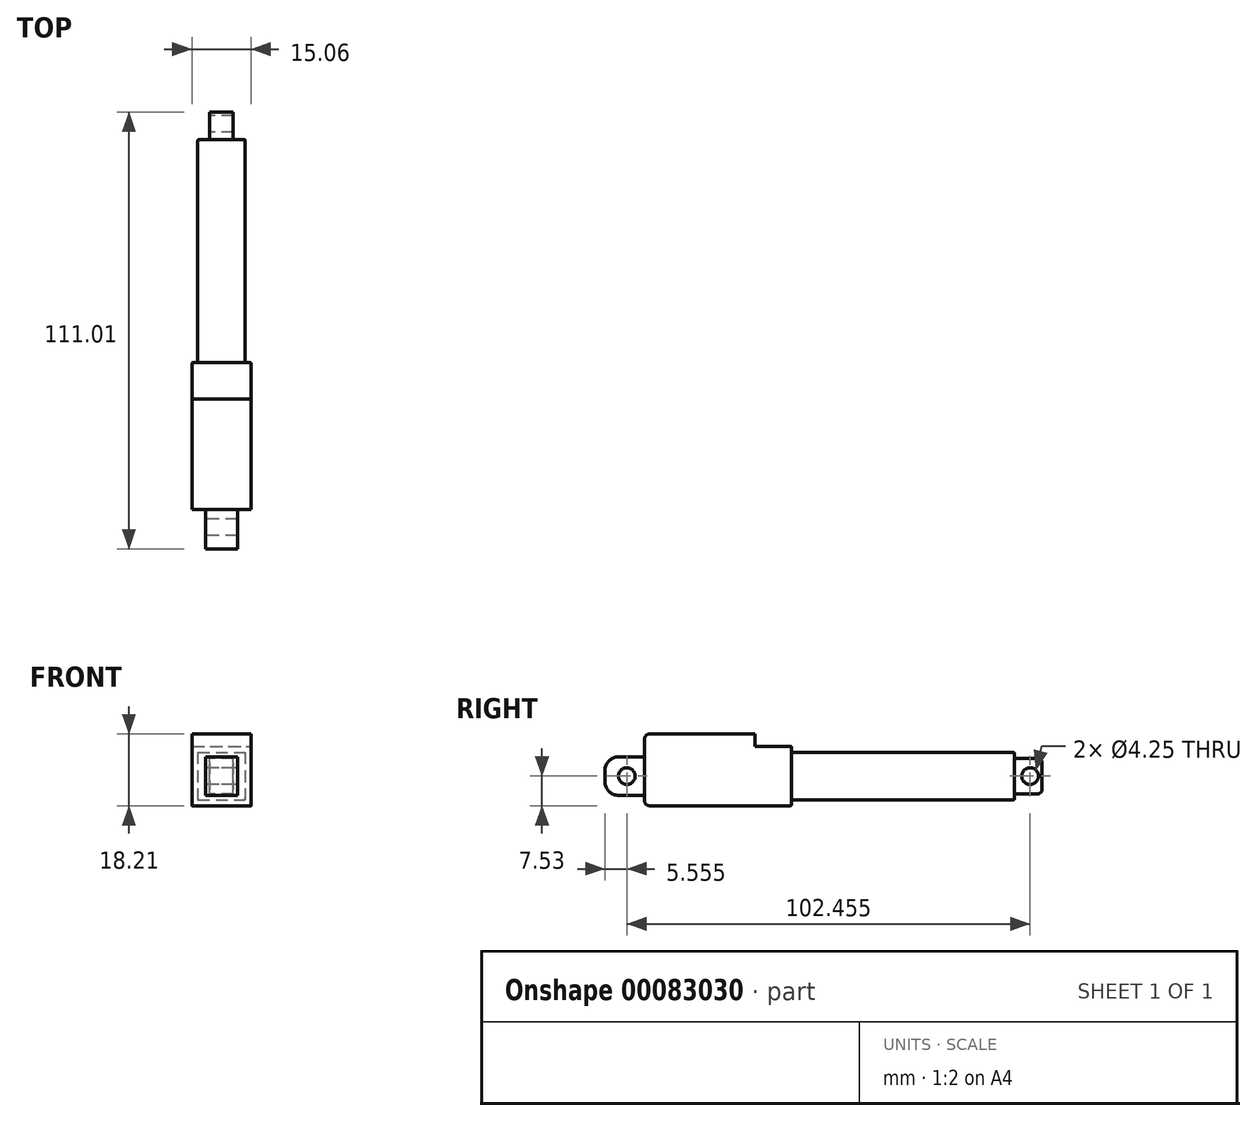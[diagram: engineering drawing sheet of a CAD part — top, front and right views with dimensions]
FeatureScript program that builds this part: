
annotation { "Feature Type Name" : "Feature", "Feature Type Description" : "" }
export const myFeature = defineFeature(function(context is Context, id is Id, definition is map)
    precondition{}
    {
        {
            var Q0;
            Q0=qCreatedBy(makeId("Front.planeOp"),FACE);
            var sketch = newSketch(context, id + "F0", { "sketchPlane" : qUnion([Q0])});
            skLineSegment(sketch, "E0.bottom", {"start": v(-6.03, 6.03) * mm, "end": v(6.03, 6.03) * mm});
            skLineSegment(sketch, "E0.top", {"start": v(-6.03, -6.03) * mm, "end": v(6.03, -6.03) * mm});
            skLineSegment(sketch, "E0.left", {"start": v(-6.03, 6.03) * mm, "end": v(-6.03, -6.03) * mm});
            skLineSegment(sketch, "E0.right", {"start": v(6.03, 6.03) * mm, "end": v(6.03, -6.03) * mm});
            skSolve(sketch);
        }
        {
            var Q0;
            Q0=makeQuery(id+"F0.imprint","IMPRINT",FACE,{"disambiguationData":[TD([[makeQuery(id+"F0.imprint","IMPRINT",EDGE,{"derivedFrom":sQuery(id+"F0.wireOp",EDGE,"E0.bottom")}),-1.0]])]});
            extrude(context, id + "F1", {"entities" : qUnion([Q0]), "depth" : 56.64 * mm});
        }
        {
            var Q0;
            Q0=makeQuery(id+"F1.opExtrude","CAP_FACE",FACE,{"disambiguationData":[OSD([sQuery(id+"F0.wireOp",EDGE,"E0.bottom"),sQuery(id+"F0.wireOp",EDGE,"E0.top"),sQuery(id+"F0.wireOp",EDGE,"E0.left"),sQuery(id+"F0.wireOp",EDGE,"E0.right")])],"isStart":false});
            var sketch = newSketch(context, id + "F2", { "sketchPlane" : qUnion([Q0])});
            skLineSegment(sketch, "E1.bottom", {"start": v(-7.53, 7.53) * mm, "end": v(7.53, 7.53) * mm});
            skLineSegment(sketch, "E1.top", {"start": v(-7.53, -7.53) * mm, "end": v(7.53, -7.53) * mm});
            skLineSegment(sketch, "E1.left", {"start": v(-7.53, 7.53) * mm, "end": v(-7.53, -7.53) * mm});
            skLineSegment(sketch, "E1.right", {"start": v(7.53, 7.53) * mm, "end": v(7.53, -7.53) * mm});
            skSolve(sketch);
        }
        {
            var Q0;
            Q0=makeQuery(id+"F2.imprint","IMPRINT",FACE,{"disambiguationData":[TD([[makeQuery(id+"F2.imprint","IMPRINT",EDGE,{"derivedFrom":sQuery(id+"F2.wireOp",EDGE,"E1.bottom")}),-1.0]])]});
            var Q1;
            Q1=makeQuery(id+"F2.imprint","IMPRINT",FACE,{"disambiguationData":[TD([[makeQuery(id+"F2.imprint","IMPRINT",EDGE,{"derivedFrom":makeQuery(id+"F1.opExtrude","CAP_EDGE",EDGE,{"disambiguationData":[OSD([sQuery(id+"F0.wireOp",EDGE,"E0.bottom")])],"isStart":false})}),-1.0]])]});
            extrude(context, id + "F3", {"entities" : qUnion([Q0, Q1]), "operationType" : NewBodyOperationType.ADD, "depth" : 37.31 * mm});
        }
        {
            var Q0;
            Q0=makeQuery(id+"F3.opExtrude","CAP_FACE",FACE,{"disambiguationData":[OSD([sQuery(id+"F2.wireOp",EDGE,"E1.bottom"),sQuery(id+"F2.wireOp",EDGE,"E1.top"),sQuery(id+"F2.wireOp",EDGE,"E1.left"),sQuery(id+"F2.wireOp",EDGE,"E1.right")])],"isStart":true});
            var sketch = newSketch(context, id + "F4", { "sketchPlane" : qUnion([Q0])});
            skLineSegment(sketch, "E2.bottom", {"start": v(-7.53, 7.53) * mm, "end": v(7.53, 7.53) * mm});
            skLineSegment(sketch, "E2.top", {"start": v(-7.53, 10.68) * mm, "end": v(7.53, 10.68) * mm});
            skLineSegment(sketch, "E2.left", {"start": v(-7.53, 7.53) * mm, "end": v(-7.53, 10.68) * mm});
            skLineSegment(sketch, "E2.right", {"start": v(7.53, 7.53) * mm, "end": v(7.53, 10.68) * mm});
            skSolve(sketch);
        }
        {
            var Q0;
            Q0=makeQuery(id+"F4.imprint","IMPRINT",FACE,{"disambiguationData":[TD([[makeQuery(id+"F4.imprint","IMPRINT",EDGE,{"derivedFrom":sQuery(id+"F4.wireOp",EDGE,"E2.bottom")}),-1.0]])]});
            var Q1;
            Q1=makeQuery(id+"F3.opExtrude","CAP_FACE",FACE,{"disambiguationData":[OSD([sQuery(id+"F2.wireOp",EDGE,"E1.bottom"),sQuery(id+"F2.wireOp",EDGE,"E1.top"),sQuery(id+"F2.wireOp",EDGE,"E1.left"),sQuery(id+"F2.wireOp",EDGE,"E1.right")])],"isStart":false});
            extrude(context, id + "F5", {"entities" : qUnion([Q0]), "operationType" : NewBodyOperationType.ADD, "endBound" : BoundingType.UP_TO_SURFACE, "oppositeDirection" : true, "endBoundEntityFace" : qUnion([Q1]), "depth" : 25.4 * mm});
        }
        {
            var Q0;
            Q0=makeQuery(id+"F5.boolean.opBoolean","MERGE",FACE,{"derivedFrom":[makeQuery(id+"F3.opExtrude","SWEPT_FACE",FACE,{"disambiguationData":[OSD([sQuery(id+"F2.wireOp",EDGE,"E1.right")])]}),makeQuery(id+"F5.opExtrude","SWEPT_FACE",FACE,{"disambiguationData":[OSD([sQuery(id+"F4.wireOp",EDGE,"E2.left")])]})]});
            var sketch = newSketch(context, id + "F6", { "sketchPlane" : qUnion([Q0])});
            skPoint(sketch, "E3.0", {"position": v(-56.64, 6.03) * mm});
            skPoint(sketch, "E4.0", {"position": v(-56.64, 10.68) * mm});
            skLineSegment(sketch, "E5", {"start": v(-65.84, 10.68) * mm, "end": v(-65.84, 7.53) * mm});
            skPoint(sketch, "E6.0", {"position": v(-56.64, -6.03) * mm});
            skPoint(sketch, "E7.0", {"position": v(-56.64, -7.53) * mm});
            skPoint(sketch, "E8", {"position": v(-56.64, 7.53) * mm});
            skLineSegment(sketch, "E9", {"start": v(-65.84, 7.53) * mm, "end": v(-56.64, 7.53) * mm});
            skPoint(sketch, "E9.startSnap0", {"position": v(-65.84, 8.36) * mm});
            skLineSegment(sketch, "E10", {"start": v(-56.64, 7.53) * mm, "end": v(-56.64, 10.68) * mm});
            skLineSegment(sketch, "E11", {"start": v(-56.64, 10.68) * mm, "end": v(-65.84, 10.68) * mm});
            skPoint(sketch, "E12.start.orphan", {"position": v(-65.84, 6.03) * mm});
            skSolve(sketch);
        }
        {
            var Q0;
            Q0=makeQuery(id+"F6.imprint","IMPRINT",FACE,{"disambiguationData":[TD([[makeQuery(id+"F6.imprint","IMPRINT",EDGE,{"derivedFrom":sQuery(id+"F6.wireOp",EDGE,"E5")}),1.0]])]});
            extrude(context, id + "F7", {"entities" : qUnion([Q0]), "operationType" : NewBodyOperationType.REMOVE, "oppositeDirection" : true, "depth" : 254 * mm});
        }
        {
            var Q0;
            Q0=makeQuery(id+"F7.boolean.opBoolean","COPY",EDGE,{"derivedFrom":makeQuery(id+"F7.opExtrude","SWEPT_EDGE",EDGE,{"disambiguationData":[OSD([sQuery(id+"F2.wireOp",EDGE,"E1.right"),sQuery(id+"F4.wireOp",EDGE,"E2.left"),sQuery(id+"F6.wireOp",EDGE,"E9"),sQuery(id+"F6.wireOp",EDGE,"E10")])]})});
            var Q1;
            Q1=makeQuery(id+"F5.boolean.opBoolean","MERGE",EDGE,{"derivedFrom":[makeQuery(id+"F3.opExtrude","CAP_EDGE",EDGE,{"disambiguationData":[OSD([sQuery(id+"F2.wireOp",EDGE,"E1.right")])],"isStart":true}),makeQuery(id+"F5.opExtrude","CAP_EDGE",EDGE,{"disambiguationData":[OSD([sQuery(id+"F4.wireOp",EDGE,"E2.left")])],"isStart":true})]});
            var Q2;
            Q2=makeQuery(id+"F3.opExtrude","CAP_EDGE",EDGE,{"disambiguationData":[OSD([sQuery(id+"F2.wireOp",EDGE,"E1.top")])],"isStart":true});
            var Q3;
            Q3=makeQuery(id+"F5.boolean.opBoolean","MERGE",EDGE,{"derivedFrom":[makeQuery(id+"F3.opExtrude","CAP_EDGE",EDGE,{"disambiguationData":[OSD([sQuery(id+"F2.wireOp",EDGE,"E1.left")])],"isStart":true}),makeQuery(id+"F5.opExtrude","CAP_EDGE",EDGE,{"disambiguationData":[OSD([sQuery(id+"F4.wireOp",EDGE,"E2.right")])],"isStart":true})]});
            var Q4;
            Q4=makeQuery(id+"F1.opExtrude","CAP_EDGE",EDGE,{"disambiguationData":[OSD([sQuery(id+"F0.wireOp",EDGE,"E0.left")])],"isStart":true});
            var Q5;
            Q5=makeQuery(id+"F1.opExtrude","CAP_EDGE",EDGE,{"disambiguationData":[OSD([sQuery(id+"F0.wireOp",EDGE,"E0.bottom")])],"isStart":true});
            var Q6;
            Q6=makeQuery(id+"F1.opExtrude","CAP_EDGE",EDGE,{"disambiguationData":[OSD([sQuery(id+"F0.wireOp",EDGE,"E0.right")])],"isStart":true});
            var Q7;
            Q7=makeQuery(id+"F1.opExtrude","CAP_EDGE",EDGE,{"disambiguationData":[OSD([sQuery(id+"F0.wireOp",EDGE,"E0.top")])],"isStart":true});
            fillet(context, id + "F8", {"entities" : qUnion([Q0, Q1, Q2, Q3, Q4, Q5, Q6, Q7]), "radius" : 0.25 * mm, "tangentPropagation" : true, "allowEdgeOverflow" : false});
        }
        {
            var Q0;
            Q0=makeQuery(id+"F7.boolean.opBoolean","COPY",EDGE,{"derivedFrom":makeQuery(id+"F7.opExtrude","SWEPT_EDGE",EDGE,{"disambiguationData":[OSD([sQuery(id+"F4.wireOp",EDGE,"E2.top"),sQuery(id+"F4.wireOp",EDGE,"E2.left"),sQuery(id+"F6.wireOp",EDGE,"E5"),sQuery(id+"F6.wireOp",EDGE,"E11")])]})});
            var Q1;
            Q1=makeQuery(id+"F5.opExtrude","CAP_EDGE",EDGE,{"disambiguationData":[OSD([sQuery(id+"F4.wireOp",EDGE,"E2.top")])],"isStart":false});
            var Q2;
            Q2=makeQuery(id+"F3.opExtrude","CAP_EDGE",EDGE,{"disambiguationData":[OSD([sQuery(id+"F2.wireOp",EDGE,"E1.top")])],"isStart":false});
            fillet(context, id + "F9", {"entities" : qUnion([Q0, Q1, Q2]), "radius" : 1.27 * mm, "tangentPropagation" : true, "allowEdgeOverflow" : false});
        }
        {
            var Q0;
            Q0=makeQuery(id+"F5.boolean.opBoolean","MERGE",FACE,{"derivedFrom":[makeQuery(id+"F3.opExtrude","CAP_FACE",FACE,{"disambiguationData":[OSD([sQuery(id+"F2.wireOp",EDGE,"E1.bottom"),sQuery(id+"F2.wireOp",EDGE,"E1.top"),sQuery(id+"F2.wireOp",EDGE,"E1.left"),sQuery(id+"F2.wireOp",EDGE,"E1.right")])],"isStart":false}),makeQuery(id+"F5.opExtrude","CAP_FACE",FACE,{"disambiguationData":[OSD([sQuery(id+"F4.wireOp",EDGE,"E2.bottom"),sQuery(id+"F4.wireOp",EDGE,"E2.top"),sQuery(id+"F4.wireOp",EDGE,"E2.left"),sQuery(id+"F4.wireOp",EDGE,"E2.right")])],"isStart":false})]});
            var sketch = newSketch(context, id + "F10", { "sketchPlane" : qUnion([Q0])});
            skLineSegment(sketch, "E13.bottom", {"start": v(-4.04, 4.89) * mm, "end": v(4.04, 4.89) * mm});
            skLineSegment(sketch, "E13.top", {"start": v(-4.04, -4.89) * mm, "end": v(4.04, -4.89) * mm});
            skLineSegment(sketch, "E13.left", {"start": v(-4.04, 4.89) * mm, "end": v(-4.04, -4.89) * mm});
            skLineSegment(sketch, "E13.right", {"start": v(4.04, 4.89) * mm, "end": v(4.04, -4.89) * mm});
            skSolve(sketch);
        }
        {
            var Q0;
            Q0=makeQuery(id+"F10.imprint","IMPRINT",FACE,{"disambiguationData":[TD([[makeQuery(id+"F10.imprint","IMPRINT",EDGE,{"derivedFrom":sQuery(id+"F10.wireOp",EDGE,"E13.bottom")}),-1.0]])]});
            extrude(context, id + "F11", {"entities" : qUnion([Q0]), "operationType" : NewBodyOperationType.ADD, "depth" : 10.06 * mm});
        }
        {
            var Q0;
            Q0=makeQuery(id+"F11.opExtrude","SWEPT_FACE",FACE,{"disambiguationData":[OSD([sQuery(id+"F10.wireOp",EDGE,"E13.left")])]});
            var sketch = newSketch(context, id + "F12", { "sketchPlane" : qUnion([Q0])});
            skLineSegment(sketch, "E14.0", {"start": v(93.95, 9.41) * mm, "end": v(93.95, -6.26) * mm});
            skLineSegment(sketch, "E15", {"start": v(93.95, 0) * mm, "end": v(98.45, 0) * mm, "construction": true});
            skPoint(sketch, "E15.endSnap0", {"position": v(93.95, 0) * mm});
            skCircle(sketch, "E16", {"center": v(98.45, 0) * mm, "radius": 2.12 * mm});
            skSolve(sketch);
        }
        {
            var Q0;
            Q0=makeQuery(id+"F12.imprint","IMPRINT",FACE,{"disambiguationData":[TD([[makeQuery(id+"F12.imprint","IMPRINT",EDGE,{"derivedFrom":sQuery(id+"F12.wireOp",EDGE,"E16")}),1.0]])]});
            extrude(context, id + "F13", {"entities" : qUnion([Q0]), "operationType" : NewBodyOperationType.REMOVE, "oppositeDirection" : true, "depth" : 25 * mm});
        }
        {
            var Q0;
            Q0=makeQuery(id+"F11.opExtrude","CAP_EDGE",EDGE,{"disambiguationData":[OSD([sQuery(id+"F10.wireOp",EDGE,"E13.bottom")])],"isStart":false});
            var Q1;
            Q1=makeQuery(id+"F11.opExtrude","CAP_EDGE",EDGE,{"disambiguationData":[OSD([sQuery(id+"F10.wireOp",EDGE,"E13.top")])],"isStart":false});
            fillet(context, id + "F14", {"entities" : qUnion([Q0, Q1]), "radius" : 3.5 * mm, "tangentPropagation" : true, "allowEdgeOverflow" : false});
        }
        {
            var Q0;
            Q0=makeQuery(id+"F1.opExtrude","SWEPT_FACE",FACE,{"disambiguationData":[OSD([sQuery(id+"F0.wireOp",EDGE,"E0.left")])]});
            var sketch = newSketch(context, id + "F15", { "sketchPlane" : qUnion([Q0])});
            skArc(sketch, "E17.0.0", {"start": v(0.25, 6.03) * mm, "mid": v(0.07, 5.96) * mm, "end": v(0, 5.78) * mm});
            skLineSegment(sketch, "E17.0.1", {"start": v(0, -5.78) * mm, "end": v(0, 5.78) * mm});
            skArc(sketch, "E17.0.2", {"start": v(0, -5.78) * mm, "mid": v(0.07, -5.96) * mm, "end": v(0.25, -6.03) * mm});
            skLineSegment(sketch, "E17.0.3", {"start": v(0.25, -6.03) * mm, "end": v(0.25, 6.03) * mm});
            skLineSegment(sketch, "E18.0", {"start": v(104.01, 1.39) * mm, "end": v(104.01, -1.39) * mm});
            skCircle(sketch, "E19.0", {"center": v(98.45, 0) * mm, "radius": 2.12 * mm});
            skSolve(sketch);
        }
        {
            var Q0;
            Q0=qCreatedBy(makeId("Right.planeOp"),FACE);
            var sketch = newSketch(context, id + "F16", { "sketchPlane" : qUnion([Q0])});
            skLineSegment(sketch, "E20.0", {"start": v(0, -5.78) * mm, "end": v(0, 5.78) * mm});
            skLineSegment(sketch, "E21.bottom", {"start": v(0, 4.5) * mm, "end": v(6, 4.5) * mm});
            skLineSegment(sketch, "E21.top", {"start": v(0, -4.5) * mm, "end": v(6, -4.5) * mm});
            skLineSegment(sketch, "E21.left", {"start": v(0, 4.5) * mm, "end": v(0, -4.5) * mm});
            skLineSegment(sketch, "E21.right", {"start": v(7, 3.5) * mm, "end": v(7, -3.5) * mm});
            skPoint(sketch, "E22.0", {"position": v(-0.25, 6.03) * mm});
            skPoint(sketch, "E23.0", {"position": v(-0.25, -6.03) * mm});
            skCircle(sketch, "E24", {"center": v(4, 0) * mm, "radius": 2.12 * mm});
            skPoint(sketch, "E25.visualSharp", {"position": v(7, 4.5) * mm});
            skArc(sketch, "E25.filletArc", {"start": v(7, 3.5) * mm, "mid": v(6.7, 4.2) * mm, "end": v(6, 4.5) * mm});
            skPoint(sketch, "E26.visualSharp", {"position": v(7, -4.5) * mm});
            skArc(sketch, "E26.filletArc", {"start": v(6, -4.5) * mm, "mid": v(6.7, -4.2) * mm, "end": v(7, -3.5) * mm});
            skSolve(sketch);
        }
        {
            var Q0;
            Q0=makeQuery(id+"F16.imprint","IMPRINT",FACE,{"disambiguationData":[TD([[makeQuery(id+"F16.imprint","IMPRINT",EDGE,{"derivedFrom":sQuery(id+"F16.wireOp",EDGE,"E21.bottom")}),-1.0]])]});
            extrude(context, id + "F17", {"entities" : qUnion([Q0]), "operationType" : NewBodyOperationType.ADD, "endBound" : BoundingType.SYMMETRIC, "depth" : 6 * mm});
        }
    });
